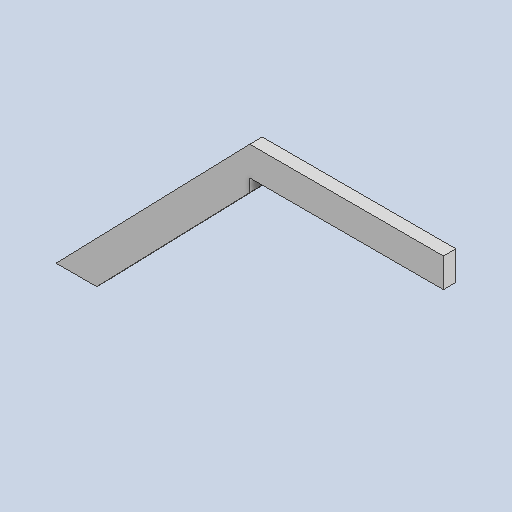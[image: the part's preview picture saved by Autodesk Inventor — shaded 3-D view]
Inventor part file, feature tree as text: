
AUTODESK INVENTOR PART (.ipt)
format: ipt  version: 2025 (Build 290162000, 162)  size: 84,480 bytes
history: native  units: in
note: dims shown in document units (in); Inventor stores cm internally (conversion verified against a paired STEP export)
features: other x3, sketch x1
ambient origin geometry x8: Origin, YZ Plane, XZ Plane, XY Plane, X Axis, Y Axis, Z Axis, Center Point
bodies: Solid1 (feature_tree)
feature tree (4):
  other  "side-side1_MIR.ipt"
  other  "Solid1::side-side1_MIR.ipt"
  other  "TaggingFeature1"
  sketch  "Sketch1"  dims[d0=0.3937in]
